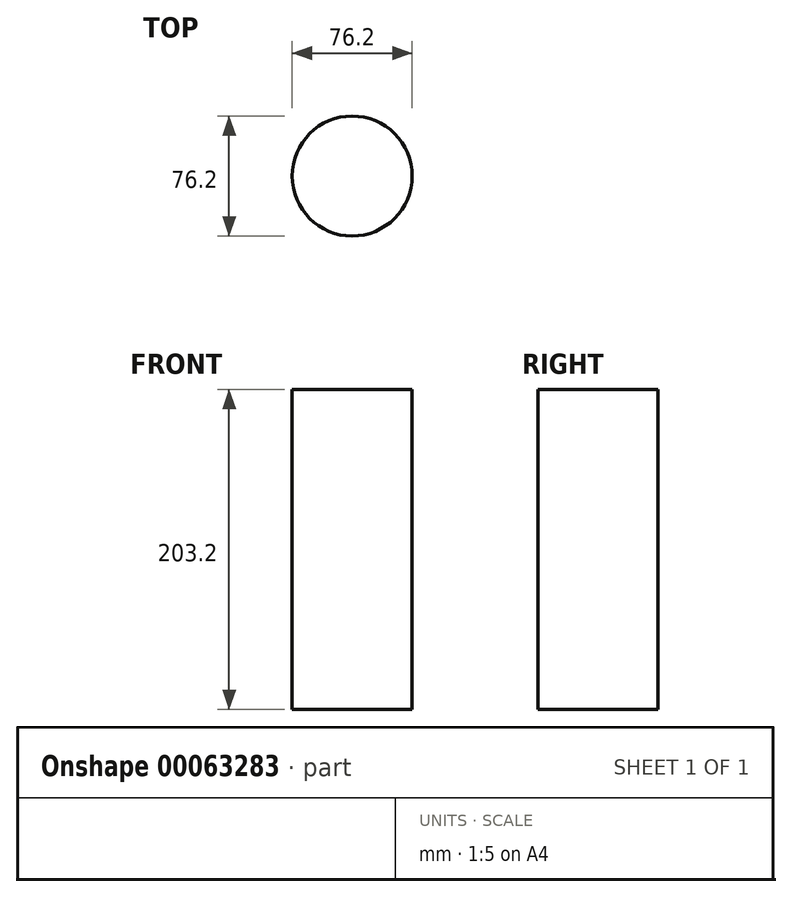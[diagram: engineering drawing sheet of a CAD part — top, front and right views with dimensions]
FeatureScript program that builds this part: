
annotation { "Feature Type Name" : "Feature", "Feature Type Description" : "" }
export const myFeature = defineFeature(function(context is Context, id is Id, definition is map)
    precondition{}
    {
        {
            var Q0;
            Q0=qCreatedBy(makeId("Top.planeOp"),FACE);
            var sketch = newSketch(context, id + "F0", { "sketchPlane" : qUnion([Q0])});
            skCircle(sketch, "E0", {"center": v(0, 0) * mm, "radius": 38.1 * mm});
            skSolve(sketch);
        }
        {
            var Q0;
            Q0 = qSketchRegion(id + "F0", true);
            extrude(context, id + "F1", {"entities" : qUnion([Q0]), "depth" : 203.2 * mm});
        }
    });
